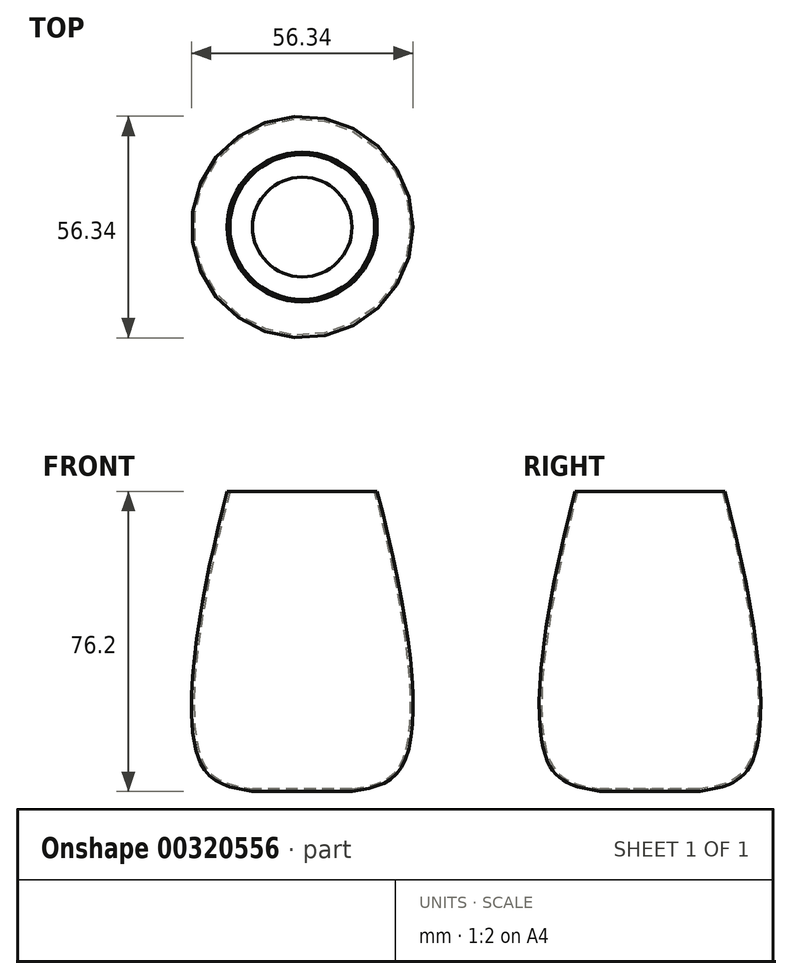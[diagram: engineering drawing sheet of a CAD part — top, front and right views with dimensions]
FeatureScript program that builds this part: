
annotation { "Feature Type Name" : "Feature", "Feature Type Description" : "" }
export const myFeature = defineFeature(function(context is Context, id is Id, definition is map)
    precondition{}
    {
        {
            var Q0;
            Q0=qCreatedBy(makeId("Front.planeOp"),FACE);
            var sketch = newSketch(context, id + "F0", { "sketchPlane" : qUnion([Q0])});
            skLineSegment(sketch, "E0", {"start": v(0, -43.73) * mm, "end": v(0, 32.47) * mm, "construction": true});
            skLineSegment(sketch, "E1", {"start": v(0, -43.73) * mm, "end": v(-12.7, -43.73) * mm, "construction": true});
            skLineSegment(sketch, "E2", {"start": v(0, -43.73) * mm, "end": v(-12.7, -43.73) * mm});
            skLineSegment(sketch, "E3", {"start": v(0, -43.73) * mm, "end": v(0, -37.38) * mm, "construction": true});
            skLineSegment(sketch, "E4", {"start": v(0, -37.38) * mm, "end": v(-25.4, -37.38) * mm, "construction": true});
            skLineSegment(sketch, "E5", {"start": v(0, 32.47) * mm, "end": v(-19.05, 32.47) * mm});
            skFitSpline(sketch, "E6", {"points": [v(-12.7, -43.73) * mm, v(-25.4, -37.38) * mm, v(-19.05, 32.47) * mm], "startDerivative": vector(-49.64, 8.02) * mm, "endDerivative": vector(33.95, 129.02) * mm});
            skLineSegment(sketch, "E7", {"start": v(0, 32.47) * mm, "end": v(0, -43.73) * mm});
            skSolve(sketch);
        }
        {
            var Q0;
            Q0=makeQuery(id+"F0.imprint","IMPRINT",FACE,{"disambiguationData":[TD([[makeQuery(id+"F0.imprint","IMPRINT",EDGE,{"derivedFrom":sQuery(id+"F0.wireOp",EDGE,"E2")}),-1.0]])]});
            var Q1;
            Q1=sQuery(id+"F0.wireOp",EDGE,"E7");
            revolve(context, id + "F1", {"entities" : qUnion([Q0]), "axis" : qUnion([Q1]), "revolveType" : RevolveType.FULL});
        }
        {
            var Q0;
            Q0=makeQuery(id+"F1.opRevolve","SWEPT_FACE",FACE,{"disambiguationData":[OSD([sQuery(id+"F0.wireOp",EDGE,"E5")])]});
            shell(context, id + "F2", {"entities" : qUnion([Q0]), "thickness" : 0.64 * mm});
        }
    });
